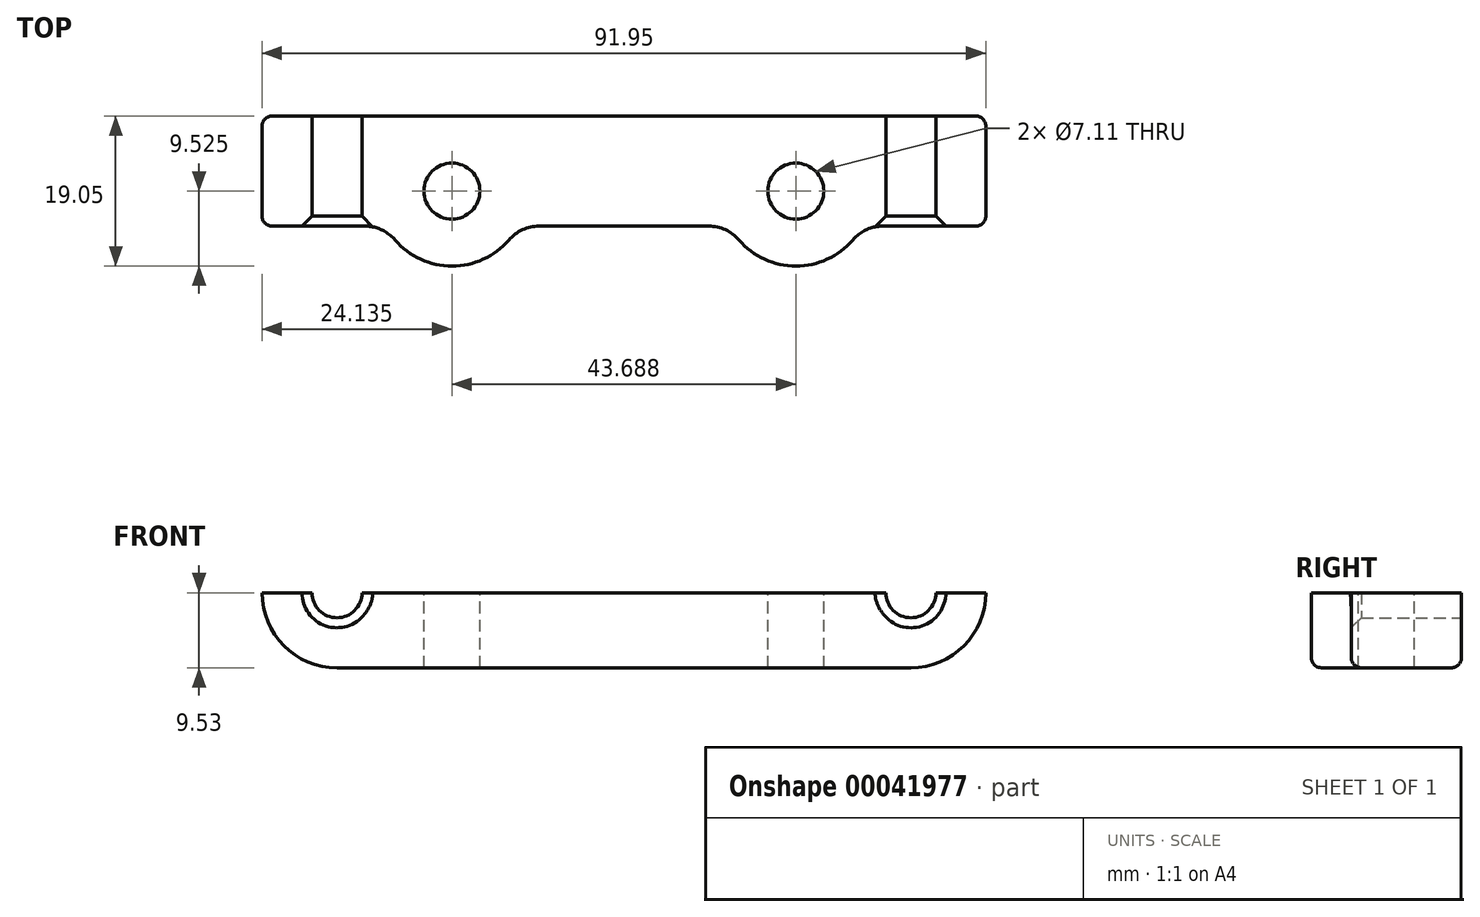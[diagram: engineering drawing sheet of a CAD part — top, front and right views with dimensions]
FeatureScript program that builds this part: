
annotation { "Feature Type Name" : "Feature", "Feature Type Description" : "" }
export const myFeature = defineFeature(function(context is Context, id is Id, definition is map)
    precondition{}
    {
        {
            var Q0;
            Q0=qCreatedBy(makeId("Front.planeOp"),FACE);
            var sketch = newSketch(context, id + "F0", { "sketchPlane" : qUnion([Q0])});
            skArc(sketch, "E0", {"start": v(-3.18, 0) * mm, "mid": v(0, -3.18) * mm, "end": v(3.18, 0) * mm});
            skArc(sketch, "E1", {"start": v(69.72, 0) * mm, "mid": v(72.9, -3.17) * mm, "end": v(76.07, 0) * mm});
            skArc(sketch, "E2", {"start": v(-9.53, 0) * mm, "mid": v(0, -9.53) * mm, "end": v(9.53, 0) * mm});
            skArc(sketch, "E3", {"start": v(63.37, 0) * mm, "mid": v(72.9, -9.52) * mm, "end": v(82.42, 0) * mm});
            skLineSegment(sketch, "E4", {"start": v(0, -9.52) * mm, "end": v(73.15, -9.52) * mm});
            skLineSegment(sketch, "E5", {"start": v(82.42, 0) * mm, "end": v(76.07, 0) * mm});
            skLineSegment(sketch, "E6.trimOffspring", {"start": v(-3.18, 0) * mm, "end": v(-9.53, 0) * mm});
            skLineSegment(sketch, "E7.trimOffspring", {"start": v(69.72, 0) * mm, "end": v(3.17, 0) * mm});
            skSolve(sketch);
        }
        {
            var Q0;
            Q0=qSketchRegion(id+"F0",true);
            extrude(context, id + "F1", {"entities" : qUnion([Q0]), "depth" : 13.97 * mm});
        }
        {
            var Q0;
            Q0=makeQuery(id+"F1.opExtrude","SWEPT_FACE",FACE,{"disambiguationData":[OSD([sQuery(id+"F0.wireOp",EDGE,"E7.trimOffspring")])]});
            var sketch = newSketch(context, id + "F2", { "sketchPlane" : qUnion([Q0])});
            skCircle(sketch, "E8", {"center": v(14.6, -9.53) * mm, "radius": 9.53 * mm});
            skCircle(sketch, "E9", {"center": v(58.3, -9.53) * mm, "radius": 9.53 * mm});
            skSolve(sketch);
        }
        {
            var Q0;
            Q0=qSketchRegion(id+"F2",true);
            var Q1;
            Q1=makeQuery(id+"F1.opExtrude","SWEPT_FACE",FACE,{"disambiguationData":[OSD([sQuery(id+"F0.wireOp",EDGE,"E4")])]});
            extrude(context, id + "F3", {"entities" : qUnion([Q0]), "operationType" : NewBodyOperationType.ADD, "endBound" : BoundingType.UP_TO_SURFACE, "oppositeDirection" : true, "endBoundEntityFace" : qUnion([Q1]), "depth" : 25.4 * mm});
        }
        {
            var Q0;
            Q0=makeQuery(id+"F3.boolean.opBoolean","MERGE",FACE,{"derivedFrom":[makeQuery(id+"F1.opExtrude","SWEPT_FACE",FACE,{"disambiguationData":[OSD([sQuery(id+"F0.wireOp",EDGE,"E7.trimOffspring")])]}),makeQuery(id+"F3.opExtrude","CAP_FACE",FACE,{"disambiguationData":[OSD([sQuery(id+"F2.wireOp",EDGE,"E8")])],"isStart":true}),makeQuery(id+"F3.opExtrude","CAP_FACE",FACE,{"disambiguationData":[OSD([sQuery(id+"F2.wireOp",EDGE,"E9")])],"isStart":true})]});
            var sketch = newSketch(context, id + "F4", { "sketchPlane" : qUnion([Q0])});
            skCircle(sketch, "E10", {"center": v(14.6, -9.53) * mm, "radius": 3.56 * mm});
            skCircle(sketch, "E11", {"center": v(58.3, -9.53) * mm, "radius": 3.56 * mm});
            skSolve(sketch);
        }
        {
            var Q0;
            Q0=qSketchRegion(id+"F4",true);
            extrude(context, id + "F5", {"entities" : qUnion([Q0]), "operationType" : NewBodyOperationType.REMOVE, "endBound" : BoundingType.THROUGH_ALL, "oppositeDirection" : true, "depth" : 25.4 * mm});
        }
        {
            var Q0;
            Q0=makeQuery(id+"F1.opExtrude","CAP_EDGE",EDGE,{"disambiguationData":[OSD([sQuery(id+"F0.wireOp",EDGE,"E0")])],"isStart":false});
            var Q1;
            Q1=makeQuery(id+"F1.opExtrude","CAP_EDGE",EDGE,{"disambiguationData":[OSD([sQuery(id+"F0.wireOp",EDGE,"E1")])],"isStart":false});
            chamfer(context, id + "F6", {"entities" : qUnion([Q0, Q1]), "width" : 1.27 * mm, "tangentPropagation" : true});
        }
        {
            var Q0;
            Q0=makeQuery(id+"F3.boolean.opBoolean","INTERSECT",EDGE,{"disambiguationData":[OD(0.0)],"derivedFrom":[makeQuery(id+"F1.opExtrude","CAP_FACE",FACE,{"disambiguationData":[OSD([sQuery(id+"F0.wireOp",EDGE,"E0"),sQuery(id+"F0.wireOp",EDGE,"E1"),sQuery(id+"F0.wireOp",EDGE,"E2"),sQuery(id+"F0.wireOp",EDGE,"E3"),sQuery(id+"F0.wireOp",EDGE,"E4"),sQuery(id+"F0.wireOp",EDGE,"E5"),sQuery(id+"F0.wireOp",EDGE,"E6.trimOffspring"),sQuery(id+"F0.wireOp",EDGE,"E7.trimOffspring")])],"isStart":false}),makeQuery(id+"F3.opExtrude","SWEPT_FACE",FACE,{"disambiguationData":[OSD([sQuery(id+"F2.wireOp",EDGE,"E8")])]})]});
            var Q1;
            Q1=makeQuery(id+"F3.boolean.opBoolean","INTERSECT",EDGE,{"disambiguationData":[OD(1.0)],"derivedFrom":[makeQuery(id+"F1.opExtrude","CAP_FACE",FACE,{"disambiguationData":[OSD([sQuery(id+"F0.wireOp",EDGE,"E0"),sQuery(id+"F0.wireOp",EDGE,"E1"),sQuery(id+"F0.wireOp",EDGE,"E2"),sQuery(id+"F0.wireOp",EDGE,"E3"),sQuery(id+"F0.wireOp",EDGE,"E4"),sQuery(id+"F0.wireOp",EDGE,"E5"),sQuery(id+"F0.wireOp",EDGE,"E6.trimOffspring"),sQuery(id+"F0.wireOp",EDGE,"E7.trimOffspring")])],"isStart":false}),makeQuery(id+"F3.opExtrude","SWEPT_FACE",FACE,{"disambiguationData":[OSD([sQuery(id+"F2.wireOp",EDGE,"E8")])]})]});
            var Q2;
            Q2=makeQuery(id+"F3.boolean.opBoolean","INTERSECT",EDGE,{"disambiguationData":[OD(1.0)],"derivedFrom":[makeQuery(id+"F1.opExtrude","CAP_FACE",FACE,{"disambiguationData":[OSD([sQuery(id+"F0.wireOp",EDGE,"E0"),sQuery(id+"F0.wireOp",EDGE,"E1"),sQuery(id+"F0.wireOp",EDGE,"E2"),sQuery(id+"F0.wireOp",EDGE,"E3"),sQuery(id+"F0.wireOp",EDGE,"E4"),sQuery(id+"F0.wireOp",EDGE,"E5"),sQuery(id+"F0.wireOp",EDGE,"E6.trimOffspring"),sQuery(id+"F0.wireOp",EDGE,"E7.trimOffspring")])],"isStart":false}),makeQuery(id+"F3.opExtrude","SWEPT_FACE",FACE,{"disambiguationData":[OSD([sQuery(id+"F2.wireOp",EDGE,"E9")])]})]});
            var Q3;
            Q3=makeQuery(id+"F3.boolean.opBoolean","INTERSECT",EDGE,{"disambiguationData":[OD(0.0)],"derivedFrom":[makeQuery(id+"F1.opExtrude","CAP_FACE",FACE,{"disambiguationData":[OSD([sQuery(id+"F0.wireOp",EDGE,"E0"),sQuery(id+"F0.wireOp",EDGE,"E1"),sQuery(id+"F0.wireOp",EDGE,"E2"),sQuery(id+"F0.wireOp",EDGE,"E3"),sQuery(id+"F0.wireOp",EDGE,"E4"),sQuery(id+"F0.wireOp",EDGE,"E5"),sQuery(id+"F0.wireOp",EDGE,"E6.trimOffspring"),sQuery(id+"F0.wireOp",EDGE,"E7.trimOffspring")])],"isStart":false}),makeQuery(id+"F3.opExtrude","SWEPT_FACE",FACE,{"disambiguationData":[OSD([sQuery(id+"F2.wireOp",EDGE,"E9")])]})]});
            fillet(context, id + "F7", {"entities" : qUnion([Q0, Q1, Q2, Q3]), "radius" : 5.08 * mm, "tangentPropagation" : true, "allowEdgeOverflow" : false});
        }
        {
            var Q0;
            {var subQ0=sQuery(id+"F2.wireOp",EDGE,"E8");var subQ1=sQuery(id+"F0.wireOp",EDGE,"E4");var subQ2=sQuery(id+"F2.wireOp",EDGE,"E9");Q0=makeQuery(id+"F3.boolean.opBoolean","SPLIT",EDGE,{"disambiguationData":[TD([makeQuery(id+"F1.opExtrude","CAP_FACE",FACE,{"disambiguationData":[OSD([sQuery(id+"F0.wireOp",EDGE,"E0"),sQuery(id+"F0.wireOp",EDGE,"E1"),sQuery(id+"F0.wireOp",EDGE,"E2"),sQuery(id+"F0.wireOp",EDGE,"E3"),subQ1,sQuery(id+"F0.wireOp",EDGE,"E5"),sQuery(id+"F0.wireOp",EDGE,"E6.trimOffspring"),sQuery(id+"F0.wireOp",EDGE,"E7.trimOffspring")])],"isStart":false}),makeQuery(id+"F1.opExtrude","SWEPT_FACE",FACE,{"disambiguationData":[OSD([subQ1])]}),makeQuery(id+"F3.opExtrude","SWEPT_FACE",FACE,{"disambiguationData":[OSD([subQ0])]}),makeQuery(id+"F3.opExtrude","CAP_FACE",FACE,{"disambiguationData":[OSD([subQ0])],"isStart":false}),makeQuery(id+"F3.opExtrude","SWEPT_FACE",FACE,{"disambiguationData":[OSD([subQ2])]}),makeQuery(id+"F3.opExtrude","CAP_FACE",FACE,{"disambiguationData":[OSD([subQ2])],"isStart":false})])],"derivedFrom":makeQuery(id+"F1.opExtrude","CAP_EDGE",EDGE,{"disambiguationData":[OSD([subQ1])],"isStart":false})});}
            var Q1;
            Q1=makeQuery(id+"F1.opExtrude","CAP_EDGE",EDGE,{"disambiguationData":[OSD([sQuery(id+"F0.wireOp",EDGE,"E4")])],"isStart":true});
            fillet(context, id + "F8", {"entities" : qUnion([Q0, Q1]), "radius" : 1.27 * mm, "tangentPropagation" : true, "allowEdgeOverflow" : false});
        }
    });
